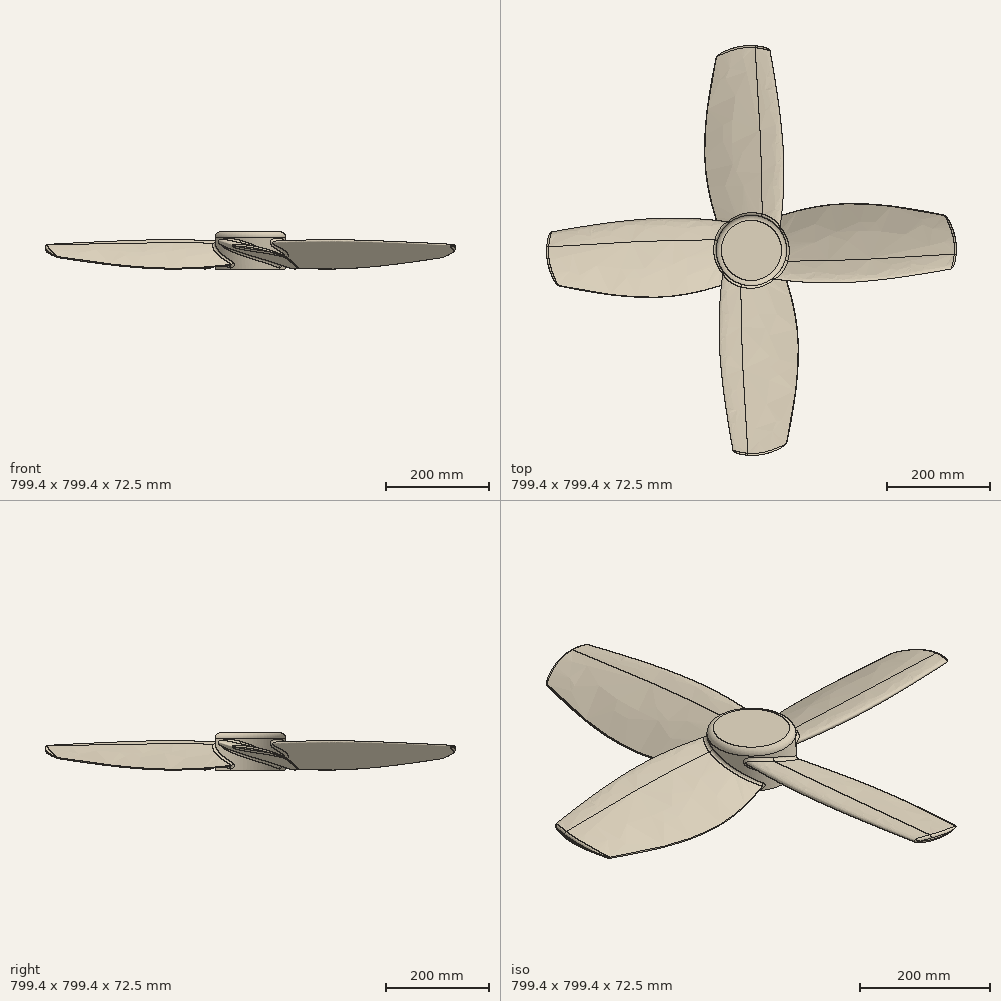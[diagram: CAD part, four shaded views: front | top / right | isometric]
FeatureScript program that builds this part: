
annotation { "Feature Type Name" : "Feature", "Feature Type Description" : "" }
export const myFeature = defineFeature(function(context is Context, id is Id, definition is map)
    precondition{}
    {
        {
            var Q0;
            Q0=qCreatedBy(makeId("Front.planeOp"),FACE);
            var sketch = newSketch(context, id + "F0", { "sketchPlane" : qUnion([Q0])});
            skLineSegment(sketch, "E0", {"start": v(-25.68, 10.16) * mm, "end": v(0, 0) * mm, "construction": true});
            skLineSegment(sketch, "E1", {"start": v(0, 0) * mm, "end": v(25.68, -10.16) * mm, "construction": true});
            skLineSegment(sketch, "E2", {"start": v(25.68, -10.16) * mm, "end": v(51.36, -20.31) * mm, "construction": true});
            skLineSegment(sketch, "E3", {"start": v(51.36, -20.31) * mm, "end": v(77.03, -30.47) * mm, "construction": true});
            skLineSegment(sketch, "E4", {"start": v(0, 0) * mm, "end": v(3.73, 9.44) * mm, "construction": true});
            skLineSegment(sketch, "E5", {"start": v(-25.68, 10.16) * mm, "end": v(-23.81, 14.88) * mm, "construction": true});
            skFitSpline(sketch, "E6", {"points": [v(-25.68, 10.16) * mm, v(3.73, 9.44) * mm, v(77.03, -30.47) * mm], "startDerivative": vector(15.03, 38) * mm, "endDerivative": vector(104.92, -93.69) * mm});
            skPoint(sketch, "E7", {"position": v(1.87, 4.72) * mm});
            skLineSegment(sketch, "E8", {"start": v(-23.81, 14.88) * mm, "end": v(1.87, 4.72) * mm, "construction": true});
            skLineSegment(sketch, "E9", {"start": v(0, 0) * mm, "end": v(-1.87, -4.72) * mm, "construction": true});
            skLineSegment(sketch, "E10", {"start": v(-25.68, 10.16) * mm, "end": v(-27.54, 5.44) * mm, "construction": true});
            skFitSpline(sketch, "E11", {"points": [v(-25.68, 10.16) * mm, v(-1.87, -4.72) * mm, v(77.03, -30.47) * mm], "startDerivative": vector(-15.23, -38.5) * mm, "endDerivative": vector(121.84, -48.19) * mm});
            skLineSegment(sketch, "E12", {"start": v(51.36, -20.31) * mm, "end": v(55.09, -10.87) * mm, "construction": true});
            skSolve(sketch);
        }
        {
            var Q0;
            Q0=qCreatedBy(makeId("Front.planeOp"),FACE);
            cPlane(context, id + "F1", {"entities" : qUnion([Q0]), "cplaneType" : CPlaneType.OFFSET, "offset" : 125 * mm, "width" : 150 * mm, "height" : 150 * mm});
        }
        {
            var Q0;
            Q0=qCreatedBy(id+"F1.planeOp",FACE);
            var sketch = newSketch(context, id + "F2", { "sketchPlane" : qUnion([Q0])});
            skLineSegment(sketch, "E13", {"start": v(-38.33, 14.06) * mm, "end": v(0, 0) * mm, "construction": true});
            skLineSegment(sketch, "E14", {"start": v(0, 0) * mm, "end": v(38.33, -14.06) * mm, "construction": true});
            skLineSegment(sketch, "E15", {"start": v(38.33, -14.06) * mm, "end": v(76.67, -28.12) * mm, "construction": true});
            skLineSegment(sketch, "E16", {"start": v(76.67, -28.12) * mm, "end": v(115, -42.17) * mm, "construction": true});
            skLineSegment(sketch, "E17", {"start": v(0, 0) * mm, "end": v(4.06, 11.06) * mm, "construction": true});
            skLineSegment(sketch, "E18", {"start": v(-38.33, 14.06) * mm, "end": v(-36.3, 19.59) * mm, "construction": true});
            skFitSpline(sketch, "E19", {"points": [v(-38.33, 14.06) * mm, v(4.06, 11.06) * mm, v(115, -42.17) * mm], "startDerivative": vector(16.44, 44.82) * mm, "endDerivative": vector(163.27, -119.63) * mm});
            skPoint(sketch, "E20", {"position": v(2.03, 5.53) * mm});
            skLineSegment(sketch, "E21", {"start": v(-36.3, 19.59) * mm, "end": v(2.03, 5.53) * mm, "construction": true});
            skLineSegment(sketch, "E22", {"start": v(0, 0) * mm, "end": v(-2.03, -5.53) * mm, "construction": true});
            skLineSegment(sketch, "E23", {"start": v(-38.33, 14.06) * mm, "end": v(-40.36, 8.53) * mm, "construction": true});
            skFitSpline(sketch, "E24", {"points": [v(-38.33, 14.06) * mm, v(-2.03, -5.53) * mm, v(115, -42.17) * mm], "startDerivative": vector(-16.57, -45.19) * mm, "endDerivative": vector(181.7, -66.64) * mm});
            skLineSegment(sketch, "E25", {"start": v(76.67, -28.12) * mm, "end": v(80.72, -17.06) * mm, "construction": true});
            skSolve(sketch);
        }
        {
            var Q0;
            Q0=qCreatedBy(makeId("Front.planeOp"),FACE);
            cPlane(context, id + "F3", {"entities" : qUnion([Q0]), "cplaneType" : CPlaneType.OFFSET, "offset" : 400 * mm, "width" : 150 * mm, "height" : 150 * mm});
        }
        {
            var Q0;
            Q0=qCreatedBy(id+"F3.planeOp",FACE);
            var sketch = newSketch(context, id + "F4", { "sketchPlane" : qUnion([Q0])});
            skLineSegment(sketch, "E26", {"start": v(-10.03, 5.14) * mm, "end": v(16.27, 0) * mm, "construction": true});
            skLineSegment(sketch, "E27", {"start": v(16.27, 0) * mm, "end": v(42.56, -5.14) * mm, "construction": true});
            skLineSegment(sketch, "E28", {"start": v(42.56, -5.14) * mm, "end": v(68.86, -10.28) * mm, "construction": true});
            skLineSegment(sketch, "E29", {"start": v(68.86, -10.28) * mm, "end": v(95.16, -15.42) * mm, "construction": true});
            skLineSegment(sketch, "E30", {"start": v(16.27, 0) * mm, "end": v(17.61, 6.9) * mm, "construction": true});
            skLineSegment(sketch, "E31", {"start": v(-10.03, 5.14) * mm, "end": v(-9.36, 8.59) * mm, "construction": true});
            skFitSpline(sketch, "E32", {"points": [v(-10.03, 5.14) * mm, v(17.61, 6.9) * mm, v(95.16, -15.42) * mm], "startDerivative": vector(5.47, 28.01) * mm, "endDerivative": vector(118.7, -57.28) * mm});
            skPoint(sketch, "E33", {"position": v(16.94, 3.45) * mm});
            skLineSegment(sketch, "E34", {"start": v(-9.36, 8.59) * mm, "end": v(16.94, 3.45) * mm, "construction": true});
            skLineSegment(sketch, "E35", {"start": v(16.27, 0) * mm, "end": v(15.6, -3.45) * mm, "construction": true});
            skLineSegment(sketch, "E36", {"start": v(-10.03, 5.14) * mm, "end": v(-10.7, 1.7) * mm, "construction": true});
            skFitSpline(sketch, "E37", {"points": [v(-10.03, 5.14) * mm, v(15.6, -3.45) * mm, v(95.16, -15.42) * mm], "startDerivative": vector(-5.51, -28.2) * mm, "endDerivative": vector(124.61, -24.36) * mm});
            skLineSegment(sketch, "E38", {"start": v(68.86, -10.28) * mm, "end": v(70.2, -3.38) * mm, "construction": true});
            skSolve(sketch);
        }
        {
            var Q0;
            Q0=qSketchRegion(id+"F0",true);
            var Q1;
            Q1=qSketchRegion(id+"F2",true);
            var Q2;
            Q2=qSketchRegion(id+"F4",true);
            var Q3;
            Q3=sQuery(id+"F0.wireOp",VERTEX,"E6.1.internal");
            var Q4;
            Q4=sQuery(id+"F2.wireOp",VERTEX,"E19.1.internal");
            var Q5;
            Q5=sQuery(id+"F4.wireOp",VERTEX,"E30.end");
            loft(context, id + "F5", {"sheetProfilesArray" : [{ "sheetProfileEntities" : qUnion([Q0]) }, { "sheetProfileEntities" : qUnion([Q1]) }, { "sheetProfileEntities" : qUnion([Q2]) }], "matchConnections" : true, "connections" : [{ "connectionEntities" : qUnion([Q3, Q4, Q5]), "connectionEdgeQueries" : qUnion([]), "connectionEdgeParameters" : [] }]});
        }
        {
            var Q0;
            Q0=qCreatedBy(makeId("Top.planeOp"),FACE);
            var sketch = newSketch(context, id + "F6", { "sketchPlane" : qUnion([Q0])});
            skFitSpline(sketch, "E39", {"points": [v(-55.98, -360.47) * mm, v(39.38, -398.87) * mm, v(142.8, -333.19) * mm], "startDerivative": vector(111.22, -150.8) * mm, "endDerivative": vector(54.24, 145.78) * mm});
            skLineSegment(sketch, "E40", {"start": v(-55.98, -360.47) * mm, "end": v(-55.98, -458.75) * mm});
            skLineSegment(sketch, "E41", {"start": v(142.8, -333.19) * mm, "end": v(142.8, -458.75) * mm});
            skLineSegment(sketch, "E42", {"start": v(142.8, -458.75) * mm, "end": v(-55.98, -458.75) * mm});
            skSolve(sketch);
        }
        {
            var Q0;
            Q0=qSketchRegion(id+"F6",true);
            extrude(context, id + "F7", {"entities" : qUnion([Q0]), "operationType" : NewBodyOperationType.REMOVE, "endBound" : BoundingType.SYMMETRIC, "oppositeDirection" : true, "depth" : 40.17 * mm});
        }
        {
            var Q0;
            Q0=makeQuery(id+"F5.opLoft","SWEPT_EDGE",EDGE,{"disambiguationData":[OSD([sQuery(id+"F2.wireOp",EDGE,"E19"),sQuery(id+"F2.wireOp",EDGE,"E24"),sQuery(id+"F4.wireOp",EDGE,"E32"),sQuery(id+"F4.wireOp",EDGE,"E37")])]});
            fillet(context, id + "F8", {"entities" : qUnion([Q0]), "radius" : 1 * mm, "tangentPropagation" : true, "allowEdgeOverflow" : false});
        }
        {
            var Q0;
            Q0=makeQuery(id+"F7.boolean.opBoolean","COPY",FACE,{"derivedFrom":makeQuery(id+"F7.opExtrude","SWEPT_FACE",FACE,{"disambiguationData":[OSD([sQuery(id+"F6.wireOp",EDGE,"E39")])]})});
            fillet(context, id + "F9", {"entities" : qUnion([Q0]), "radius" : 4 * mm, "tangentPropagation" : true, "allowEdgeOverflow" : false});
        }
        {
            var Q0;
            Q0=qCreatedBy(makeId("Top.planeOp"),FACE);
            var sketch = newSketch(context, id + "F10", { "sketchPlane" : qUnion([Q0])});
            skCircle(sketch, "E43", {"center": v(24.35, 0) * mm, "radius": 68.6 * mm});
            skSolve(sketch);
        }
        {
            var Q0;
            Q0=qSketchRegion(id+"F10",true);
            extrude(context, id + "F11", {"entities" : qUnion([Q0]), "depth" : 32.31 * mm, "hasSecondDirection" : true, "secondDirectionOppositeDirection" : true, "secondDirectionDepth" : 40 * mm});
        }
        {
            var Q0;
            Q0=makeQuery(id+"F5.opLoft","SWEPT_BODY",BODY,{"disambiguationData":[OSD([makeQuery(id+"F0.imprint","IMPRINT",FACE,{"disambiguationData":[TD([[makeQuery(id+"F0.imprint","IMPRINT",EDGE,{"derivedFrom":sQuery(id+"F0.wireOp",EDGE,"E6")}),-1.0]])]}),sQuery(id+"F2.wireOp",EDGE,"E24"),makeQuery(id+"F4.imprint","IMPRINT",FACE,{"disambiguationData":[TD([[makeQuery(id+"F4.imprint","IMPRINT",EDGE,{"derivedFrom":sQuery(id+"F4.wireOp",EDGE,"E32")}),-1.0]])]})])]});
            var Q1;
            Q1=makeQuery(id+"F11.opExtrude","SWEPT_FACE",FACE,{"disambiguationData":[OSD([sQuery(id+"F10.wireOp",EDGE,"E43")])]});
            circularPattern(context, id + "F12", {"entities" : qUnion([Q0]), "axis" : qUnion([Q1]), "angle" : 360 * degree, "instanceCount" : 4, "equalSpace" : true});
        }
        {
            var Q0;
            Q0=makeQuery(id+"F12.opPattern","COPY",BODY,{"derivedFrom":makeQuery(id+"F5.opLoft","SWEPT_BODY",BODY,{"disambiguationData":[OSD([makeQuery(id+"F0.imprint","IMPRINT",FACE,{"disambiguationData":[TD([[makeQuery(id+"F0.imprint","IMPRINT",EDGE,{"derivedFrom":sQuery(id+"F0.wireOp",EDGE,"E6")}),-1.0]])]}),sQuery(id+"F2.wireOp",EDGE,"E24"),makeQuery(id+"F4.imprint","IMPRINT",FACE,{"disambiguationData":[TD([[makeQuery(id+"F4.imprint","IMPRINT",EDGE,{"derivedFrom":sQuery(id+"F4.wireOp",EDGE,"E32")}),-1.0]])]})])]}),"instanceName":"2"});
            var Q1;
            Q1=makeQuery(id+"F5.opLoft","SWEPT_BODY",BODY,{"disambiguationData":[OSD([makeQuery(id+"F0.imprint","IMPRINT",FACE,{"disambiguationData":[TD([[makeQuery(id+"F0.imprint","IMPRINT",EDGE,{"derivedFrom":sQuery(id+"F0.wireOp",EDGE,"E6")}),-1.0]])]}),sQuery(id+"F2.wireOp",EDGE,"E24"),makeQuery(id+"F4.imprint","IMPRINT",FACE,{"disambiguationData":[TD([[makeQuery(id+"F4.imprint","IMPRINT",EDGE,{"derivedFrom":sQuery(id+"F4.wireOp",EDGE,"E32")}),-1.0]])]})])]});
            var Q2;
            Q2=makeQuery(id+"F11.opExtrude","SWEPT_BODY",BODY,{"disambiguationData":[OSD([sQuery(id+"F10.wireOp",EDGE,"E43")])]});
            var Q3;
            Q3=makeQuery(id+"F12.opPattern","COPY",BODY,{"derivedFrom":makeQuery(id+"F5.opLoft","SWEPT_BODY",BODY,{"disambiguationData":[OSD([makeQuery(id+"F0.imprint","IMPRINT",FACE,{"disambiguationData":[TD([[makeQuery(id+"F0.imprint","IMPRINT",EDGE,{"derivedFrom":sQuery(id+"F0.wireOp",EDGE,"E6")}),-1.0]])]}),sQuery(id+"F2.wireOp",EDGE,"E24"),makeQuery(id+"F4.imprint","IMPRINT",FACE,{"disambiguationData":[TD([[makeQuery(id+"F4.imprint","IMPRINT",EDGE,{"derivedFrom":sQuery(id+"F4.wireOp",EDGE,"E32")}),-1.0]])]})])]}),"instanceName":"1"});
            var Q4;
            Q4=makeQuery(id+"F12.opPattern","COPY",BODY,{"derivedFrom":makeQuery(id+"F5.opLoft","SWEPT_BODY",BODY,{"disambiguationData":[OSD([makeQuery(id+"F0.imprint","IMPRINT",FACE,{"disambiguationData":[TD([[makeQuery(id+"F0.imprint","IMPRINT",EDGE,{"derivedFrom":sQuery(id+"F0.wireOp",EDGE,"E6")}),-1.0]])]}),sQuery(id+"F2.wireOp",EDGE,"E24"),makeQuery(id+"F4.imprint","IMPRINT",FACE,{"disambiguationData":[TD([[makeQuery(id+"F4.imprint","IMPRINT",EDGE,{"derivedFrom":sQuery(id+"F4.wireOp",EDGE,"E32")}),-1.0]])]})])]}),"instanceName":"4"});
            var Q5;
            Q5=makeQuery(id+"F12.opPattern","COPY",BODY,{"derivedFrom":makeQuery(id+"F5.opLoft","SWEPT_BODY",BODY,{"disambiguationData":[OSD([makeQuery(id+"F0.imprint","IMPRINT",FACE,{"disambiguationData":[TD([[makeQuery(id+"F0.imprint","IMPRINT",EDGE,{"derivedFrom":sQuery(id+"F0.wireOp",EDGE,"E6")}),-1.0]])]}),sQuery(id+"F2.wireOp",EDGE,"E24"),makeQuery(id+"F4.imprint","IMPRINT",FACE,{"disambiguationData":[TD([[makeQuery(id+"F4.imprint","IMPRINT",EDGE,{"derivedFrom":sQuery(id+"F4.wireOp",EDGE,"E32")}),-1.0]])]})])]}),"instanceName":"3"});
            booleanBodies(context, id + "F13", {"operationType" : BooleanOperationType.UNION, "tools" : qUnion([Q0, Q1, Q2, Q3, Q4, Q5])});
        }
        {
            var Q0;
            {var subQ0=sQuery(id+"F0.wireOp",VERTEX,"E6.1.internal");var subQ1=sQuery(id+"F0.wireOp",EDGE,"E6");var subQ2=sQuery(id+"F0.wireOp",EDGE,"E11");var subQ3=sQuery(id+"F2.wireOp",VERTEX,"E19.1.internal");var subQ4=sQuery(id+"F2.wireOp",EDGE,"E19");var subQ5=sQuery(id+"F2.wireOp",EDGE,"E24");Q0=makeQuery(id+"F13.opBoolean","INTERSECT",EDGE,{"derivedFrom":[makeQuery(id+"F11.opExtrude","SWEPT_FACE",FACE,{"disambiguationData":[OSD([sQuery(id+"F10.wireOp",EDGE,"E43")])]}),makeQuery(id+"F12.opPattern","COPY",FACE,{"derivedFrom":makeQuery(id+"F5.opLoft","SWEPT_FACE",FACE,{"disambiguationData":[OSD([subQ0,subQ1,subQ2,subQ3,subQ4,subQ5]),TDD([subQ0,makeQuery(id+"F0.imprint","INTERSECT",VERTEX,{"disambiguationData":[OD(0.0)],"derivedFrom":[subQ1,subQ2]}),makeQuery(id+"F0.imprint","IMPRINT",EDGE,{"derivedFrom":subQ1}),subQ3,makeQuery(id+"F2.imprint","INTERSECT",VERTEX,{"disambiguationData":[OD(0.0)],"derivedFrom":[subQ4,subQ5]}),makeQuery(id+"F2.imprint","IMPRINT",EDGE,{"derivedFrom":subQ4})])]}),"instanceName":"2"})]});}
            var Q1;
            {var subQ0=sQuery(id+"F0.wireOp",VERTEX,"E6.1.internal");var subQ1=sQuery(id+"F0.wireOp",EDGE,"E6");var subQ2=sQuery(id+"F0.wireOp",EDGE,"E11");var subQ3=sQuery(id+"F2.wireOp",VERTEX,"E19.1.internal");var subQ4=sQuery(id+"F2.wireOp",EDGE,"E19");var subQ5=sQuery(id+"F2.wireOp",EDGE,"E24");Q1=makeQuery(id+"F13.opBoolean","INTERSECT",EDGE,{"derivedFrom":[makeQuery(id+"F5.opLoft","SWEPT_FACE",FACE,{"disambiguationData":[OSD([subQ0,subQ1,subQ2,subQ3,subQ4,subQ5]),TDD([subQ0,makeQuery(id+"F0.imprint","INTERSECT",VERTEX,{"disambiguationData":[OD(1.0)],"derivedFrom":[subQ1,subQ2]}),makeQuery(id+"F0.imprint","IMPRINT",EDGE,{"derivedFrom":subQ1}),subQ3,makeQuery(id+"F2.imprint","INTERSECT",VERTEX,{"disambiguationData":[OD(1.0)],"derivedFrom":[subQ4,subQ5]}),makeQuery(id+"F2.imprint","IMPRINT",EDGE,{"derivedFrom":subQ4})])]}),makeQuery(id+"F11.opExtrude","SWEPT_FACE",FACE,{"disambiguationData":[OSD([sQuery(id+"F10.wireOp",EDGE,"E43")])]})]});}
            var Q2;
            {var subQ0=sQuery(id+"F0.wireOp",VERTEX,"E6.1.internal");var subQ1=sQuery(id+"F0.wireOp",EDGE,"E6");var subQ2=sQuery(id+"F0.wireOp",EDGE,"E11");var subQ3=sQuery(id+"F2.wireOp",VERTEX,"E19.1.internal");var subQ4=sQuery(id+"F2.wireOp",EDGE,"E19");var subQ5=sQuery(id+"F2.wireOp",EDGE,"E24");Q2=makeQuery(id+"F13.opBoolean","INTERSECT",EDGE,{"derivedFrom":[makeQuery(id+"F11.opExtrude","SWEPT_FACE",FACE,{"disambiguationData":[OSD([sQuery(id+"F10.wireOp",EDGE,"E43")])]}),makeQuery(id+"F12.opPattern","COPY",FACE,{"derivedFrom":makeQuery(id+"F5.opLoft","SWEPT_FACE",FACE,{"disambiguationData":[OSD([subQ0,subQ1,subQ2,subQ3,subQ4,subQ5]),TDD([subQ0,makeQuery(id+"F0.imprint","INTERSECT",VERTEX,{"disambiguationData":[OD(1.0)],"derivedFrom":[subQ1,subQ2]}),makeQuery(id+"F0.imprint","IMPRINT",EDGE,{"derivedFrom":subQ1}),subQ3,makeQuery(id+"F2.imprint","INTERSECT",VERTEX,{"disambiguationData":[OD(1.0)],"derivedFrom":[subQ4,subQ5]}),makeQuery(id+"F2.imprint","IMPRINT",EDGE,{"derivedFrom":subQ4})])]}),"instanceName":"1"})]});}
            var Q3;
            {var subQ0=sQuery(id+"F0.wireOp",VERTEX,"E6.1.internal");var subQ1=sQuery(id+"F0.wireOp",EDGE,"E6");var subQ2=sQuery(id+"F0.wireOp",EDGE,"E11");var subQ3=sQuery(id+"F2.wireOp",VERTEX,"E19.1.internal");var subQ4=sQuery(id+"F2.wireOp",EDGE,"E19");var subQ5=sQuery(id+"F2.wireOp",EDGE,"E24");Q3=makeQuery(id+"F13.opBoolean","INTERSECT",EDGE,{"derivedFrom":[makeQuery(id+"F11.opExtrude","SWEPT_FACE",FACE,{"disambiguationData":[OSD([sQuery(id+"F10.wireOp",EDGE,"E43")])]}),makeQuery(id+"F12.opPattern","COPY",FACE,{"derivedFrom":makeQuery(id+"F5.opLoft","SWEPT_FACE",FACE,{"disambiguationData":[OSD([subQ0,subQ1,subQ2,subQ3,subQ4,subQ5]),TDD([subQ0,makeQuery(id+"F0.imprint","INTERSECT",VERTEX,{"disambiguationData":[OD(1.0)],"derivedFrom":[subQ1,subQ2]}),makeQuery(id+"F0.imprint","IMPRINT",EDGE,{"derivedFrom":subQ1}),subQ3,makeQuery(id+"F2.imprint","INTERSECT",VERTEX,{"disambiguationData":[OD(1.0)],"derivedFrom":[subQ4,subQ5]}),makeQuery(id+"F2.imprint","IMPRINT",EDGE,{"derivedFrom":subQ4})])]}),"instanceName":"4"})]});}
            var Q4;
            {var subQ0=sQuery(id+"F0.wireOp",VERTEX,"E6.1.internal");var subQ1=sQuery(id+"F0.wireOp",EDGE,"E6");var subQ2=sQuery(id+"F0.wireOp",EDGE,"E11");var subQ3=sQuery(id+"F2.wireOp",VERTEX,"E19.1.internal");var subQ4=sQuery(id+"F2.wireOp",EDGE,"E19");var subQ5=sQuery(id+"F2.wireOp",EDGE,"E24");Q4=makeQuery(id+"F13.opBoolean","INTERSECT",EDGE,{"derivedFrom":[makeQuery(id+"F11.opExtrude","SWEPT_FACE",FACE,{"disambiguationData":[OSD([sQuery(id+"F10.wireOp",EDGE,"E43")])]}),makeQuery(id+"F12.opPattern","COPY",FACE,{"derivedFrom":makeQuery(id+"F5.opLoft","SWEPT_FACE",FACE,{"disambiguationData":[OSD([subQ0,subQ1,subQ2,subQ3,subQ4,subQ5]),TDD([subQ0,makeQuery(id+"F0.imprint","INTERSECT",VERTEX,{"disambiguationData":[OD(0.0)],"derivedFrom":[subQ1,subQ2]}),makeQuery(id+"F0.imprint","IMPRINT",EDGE,{"derivedFrom":subQ1}),subQ3,makeQuery(id+"F2.imprint","INTERSECT",VERTEX,{"disambiguationData":[OD(0.0)],"derivedFrom":[subQ4,subQ5]}),makeQuery(id+"F2.imprint","IMPRINT",EDGE,{"derivedFrom":subQ4})])]}),"instanceName":"3"})]});}
            fillet(context, id + "F15", {"entities" : qUnion([Q0, Q1, Q2, Q3, Q4]), "radius" : 5 * mm, "tangentPropagation" : true, "allowEdgeOverflow" : false});
        }
        {
            var Q0;
            Q0=makeQuery(id+"F11.opExtrude","CAP_EDGE",EDGE,{"disambiguationData":[OSD([sQuery(id+"F10.wireOp",EDGE,"E43")])],"isStart":false});
            fillet(context, id + "F16", {"entities" : qUnion([Q0]), "radius" : 10 * mm, "tangentPropagation" : true, "allowEdgeOverflow" : false});
        }
    });
